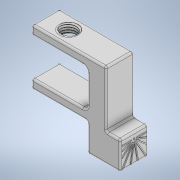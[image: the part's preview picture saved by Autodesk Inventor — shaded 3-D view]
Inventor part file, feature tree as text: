
AUTODESK INVENTOR PART (.ipt)
format: ipt  version: 2020 (Build 240168000, 168)  size: 770,048 bytes
history: native  units: mm
features: sketch x12, extrude x10, fillet x2, thread x1, revolve x1, helix x1
ambient origin geometry x8: Origin, YZ Plane, XZ Plane, XY Plane, X Axis, Y Axis, Z Axis, Center Point
bodies: Solid1 (feature_tree), Solid4 (feature_tree)
feature tree (27):
  extrude  "Extrusion1"  Depth=30.0mm
  extrude  "Extrusion2"  Depth=60.0mm
  extrude  "Extrusion3"  Depth=80.0mm TaperAngle=0.0deg
  extrude  "Extrusion4"  Depth=30.0mm
  fillet  "Fillet1"  Radius=20.0mm
  extrude  "Extrusion12"  Depth=10.0mm TaperAngle=0.0deg
  extrude  "Extrusion13"  Depth=9.599311mm
  extrude  "Extrusion14"  Depth=15.0mm TaperAngle=0.0deg
  thread  "Thread8"  [1 undecoded]
  revolve  "Revolution4"  [1 undecoded]
  helix  "Coil3"  [1 undecoded]
  fillet  "Fillet2"  Radius=2.5mm
  extrude  "Extrusion23"  TaperAngle=0.0deg  [1 undecoded]
  extrude  "Extrusion35"  Depth=10.0mm
  extrude  "Extrusion36"  Depth=9.599311mm
  sketch  "Sketch2"  dims[d0=60.0mm d1=30.0mm]
  sketch  "Sketch3"  dims[d2=80.0mm d3=0.0mm d4=60.0mm]
  sketch  "Sketch4"  dims[d5=40.0mm d6=80.0mm d7=0.0mm]
  sketch  "Sketch5"  dims[d8=20.0mm d9=30.0mm d10=20.0mm d11=0.0mm]
  sketch  "Sketch23"  dims[d12=20.0mm d13=10.0mm d14=0.0mm]
  sketch  "Sketch24"  dims[d17=5.0mm d55=9.599311mm]
  sketch  "Sketch25"  dims[d76=9.599311mm d91=15.0mm d92=0.0mm d93=5.0mm d94=0.0mm]
  sketch  "Sketch29"  dims[d95=5.0mm d96=0.0mm d103=10.0mm d104=0.0mm d105=9.599311mm d106=0.400208mm d107=0.400208mm d110=2.5mm]
  sketch  "Sketch30"  dims[d112=9.599311mm d114=0.0mm]
  sketch  "Sketch49"  dims[d115=2.5025mm d116=15.0mm d117=10.0mm d118=0.0mm d119=0.0mm d120=0.0mm d121=0.0mm d122=0.0mm d141=9.599311mm]
  sketch  "Sketch67"  dims[d166=9.599311mm d186=9.599311mm]
  sketch  "Sketch68"  dims[d197=2.0mm d207=9.599311mm d227=9.599311mm d250=9.599311mm d279=1.05mm d280=1.05mm d281=1.05mm d282=1.05mm d283=1.05mm d284=1.05mm d285=1.05mm d286=1.05mm d287=6.9mm d288=0.0mm d1059=2.0mm d1060=9.0mm d1061=0.0mm d1069=30.0mm d1074=30.0mm d1110=30.0mm d1113=30.0mm d1120=7.759mm d1121=0.7mm d1122=0.0mm d271=0.5mm d272=0.872665mm d273=0.5mm d274=0.872665mm]
note: 4 required parameter values undecoded (feature->parameter linkage not recoverable at this tier; creation-order binding heuristic only, values carry confidence <= 0.55)